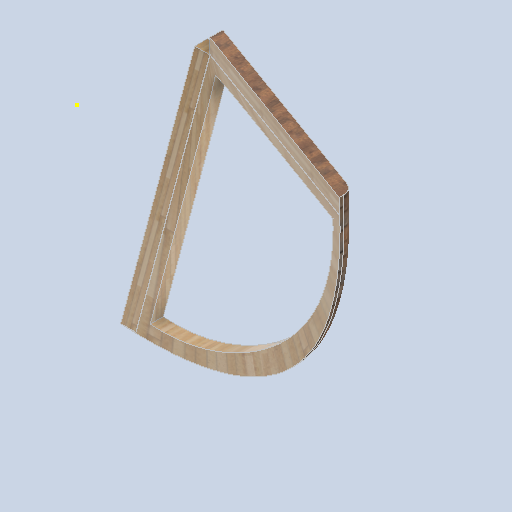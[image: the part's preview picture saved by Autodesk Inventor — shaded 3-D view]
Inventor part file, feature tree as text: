
AUTODESK INVENTOR PART (.ipt)
format: ipt  version: 2024.2 (Build 282272000, 272)  size: 292,352 bytes
history: native  units: in
note: dims shown in document units (in); Inventor stores cm internally (conversion verified against a paired STEP export)
features: sketch x12, plane x8, other x3
ambient origin geometry x8: Origin, YZ Plane, XZ Plane, XY Plane, X Axis, Y Axis, Z Axis, Center Point
bodies: Solid1 (feature_tree)
feature tree (23):
  other  "side_curve_corner_frame.ipt"
  other  "Solid1::side_curve_corner_frame.ipt"
  other  "TaggingFeature1"
  sketch  "Sketch1"  dims[d0=0.3937in]
  sketch  "Sketch2"
  sketch  "Sketch3"
  sketch  "Sketch4"
  sketch  "Sketch5"
  sketch  "Sketch6"
  sketch  "Sketch7"
  sketch  "Sketch8"
  sketch  "Sketch10"
  sketch  "Sketch11"
  sketch  "Sketch12"
  sketch  "Sketch14"
  plane  "Work Plane1"
  plane  "Work Plane2"
  plane  "Work Plane3"
  plane  "Work Plane4"
  plane  "Work Plane5"
  plane  "Work Plane6"
  plane  "Work Plane7"
  plane  "Work Plane8"
